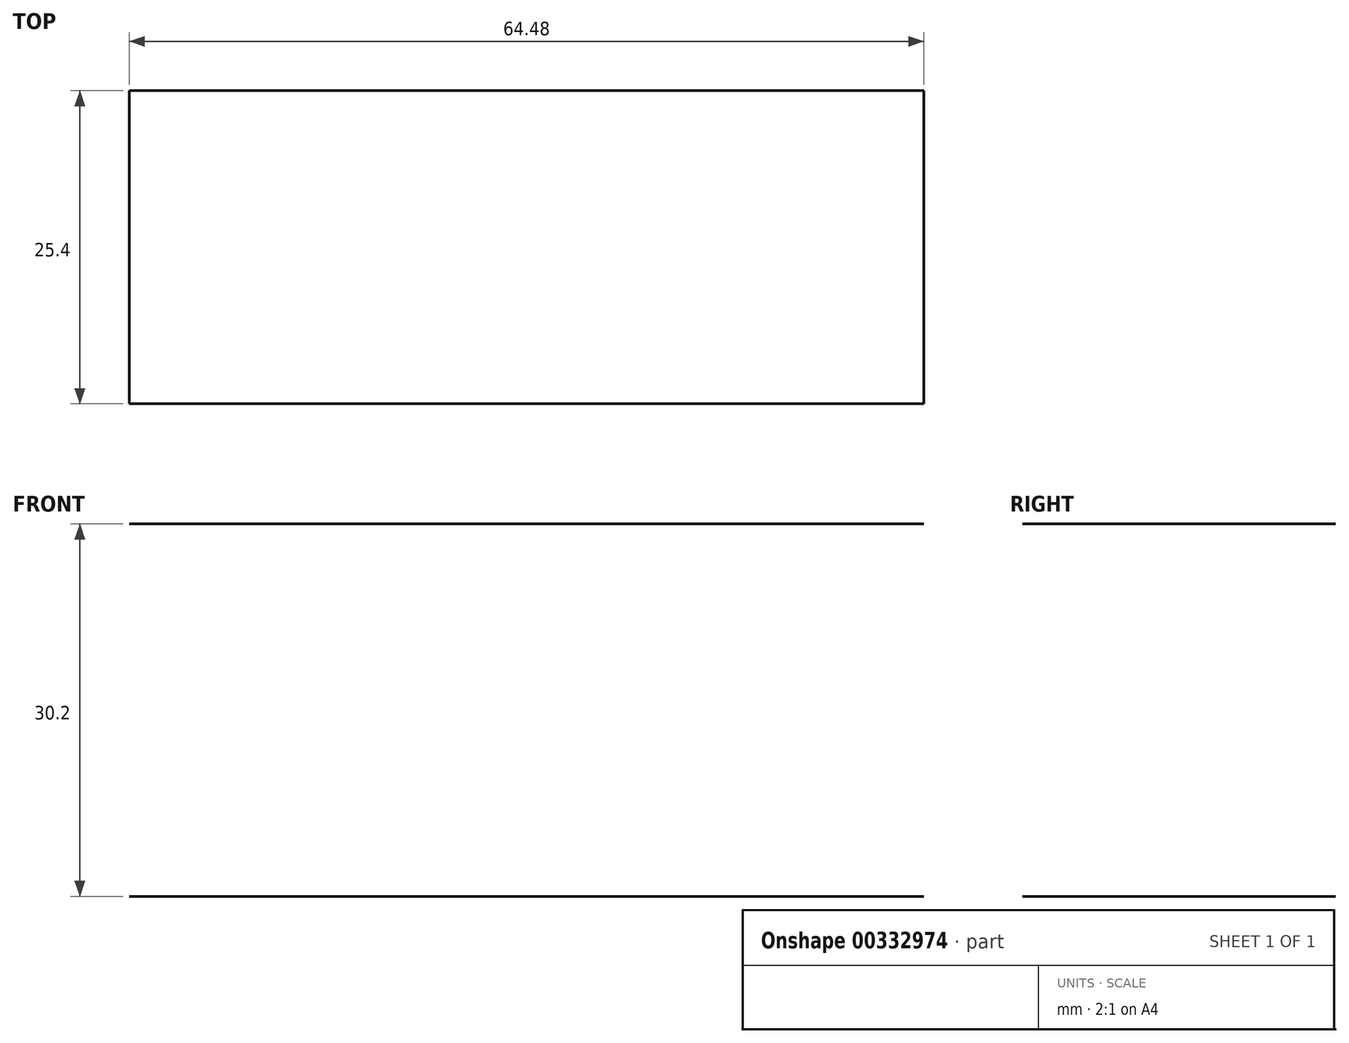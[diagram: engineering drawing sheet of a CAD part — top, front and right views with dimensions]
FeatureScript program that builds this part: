
annotation { "Feature Type Name" : "Feature", "Feature Type Description" : "" }
export const myFeature = defineFeature(function(context is Context, id is Id, definition is map)
    precondition{}
    {
        {
            var Q0;
            Q0=qCreatedBy(makeId("Front.planeOp"),FACE);
            var sketch = newSketch(context, id + "F0", { "sketchPlane" : qUnion([Q0])});
            skLineSegment(sketch, "E0.bottom", {"start": v(-3.89, 9.4) * mm, "end": v(-66.03, 9.4) * mm});
            skLineSegment(sketch, "E0.top", {"start": v(-3.89, 45.34) * mm, "end": v(-66.03, 45.34) * mm});
            skLineSegment(sketch, "E0.left", {"start": v(-3.89, 9.4) * mm, "end": v(-3.89, 45.34) * mm});
            skLineSegment(sketch, "E0.right", {"start": v(-66.03, 9.4) * mm, "end": v(-66.03, 45.34) * mm});
            skPoint(sketch, "E0.middle", {"position": v(-34.96, 27.37) * mm});
            skLineSegment(sketch, "E1.bottom", {"start": v(-32.24, 15.1) * mm, "end": v(32.24, 15.1) * mm});
            skLineSegment(sketch, "E1.top", {"start": v(-32.24, -15.1) * mm, "end": v(32.24, -15.1) * mm});
            skLineSegment(sketch, "E1.left", {"start": v(-32.24, 15.1) * mm, "end": v(-32.24, -15.1) * mm});
            skLineSegment(sketch, "E1.right", {"start": v(32.24, 15.1) * mm, "end": v(32.24, -15.1) * mm});
            skPoint(sketch, "E1.middle", {"position": v(0, 0) * mm});
            skSolve(sketch);
        }
        {
            var Q0;
            {var subQ4=sQuery(id+"F0.wireOp",EDGE,"E1.top");Q0=makeQuery(id+"F0.imprint","IMPRINT",FACE,{"disambiguationData":[TD([[makeQuery(id+"F0.imprint","IMPRINT",EDGE,{"derivedFrom":subQ4}),1.0]])]});}
            var Q1;
            Q1=sQuery(id+"F0.wireOp",EDGE,"E1.bottom");
            var Q2;
            Q2=sQuery(id+"F0.wireOp",EDGE,"E1.top");
            extrude(context, id + "F1", {"entities" : qUnion([Q0]), "bodyType" : ToolBodyType.SURFACE, "surfaceEntities" : qUnion([Q1, Q2]), "oppositeDirection" : true, "depth" : 25.4 * mm});
        }
    });
